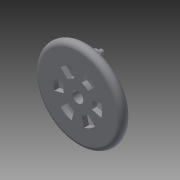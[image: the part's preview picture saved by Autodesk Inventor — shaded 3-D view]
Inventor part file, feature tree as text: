
AUTODESK INVENTOR PART (.ipt)
format: ipt  version: 2015 (Build 190159000, 159)  size: 221,184 bytes
history: native  units: in
note: dims shown in document units (in); Inventor stores cm internally (conversion verified against a paired STEP export)
features: sketch x4, extrude x3, revolve x1, fillet x1, hole x1
ambient origin geometry x8: Origin, YZ Plane, XZ Plane, XY Plane, X Axis, Y Axis, Z Axis, Center Point
bodies: Solid1 (feature_tree)
feature tree (10):
  revolve  "Revolution1"  [1 undecoded]
  fillet  "Fillet1"  Radius=0.25in
  extrude  "Extrusion1"  Depth=0.125in
  sketch  "Sketch3"  dims[d6=0.25in d9=0.5in]
  extrude  "Extrusion2"  Depth=0.5in
  extrude  "Extrusion3"  TaperAngle=90.0deg  [1 undecoded]
  hole  "Hole1"  [1 undecoded]
  sketch  "Sketch1"  dims[d0=1.0in d1=0.14in d2=0.25in]
  sketch  "Sketch2"  dims[d3=0.0in d5=0.125in]
  sketch  "Sketch4"  dims[d11=0.125in d12=90.0deg d13=0.0625in d14=0.75in d15=1.25in d16=105.0deg d17=75.0deg d18=75.0deg d19=105.0deg d20=2.3622in d22=360.0deg d24=1.0in d25=0.0in d26=0.7in d27=0.25in d28=0.7in d29=0.125in d30=0.375in d31=0.0in d32=0.5in d33=0.0in d34=0.0625in d35=0.75in d36=0.375in d37=0.25in d38=0.5635in d39=0.25in d40=0.8108in]
note: 3 required parameter values undecoded (feature->parameter linkage not recoverable at this tier; creation-order binding heuristic only, values carry confidence <= 0.55)